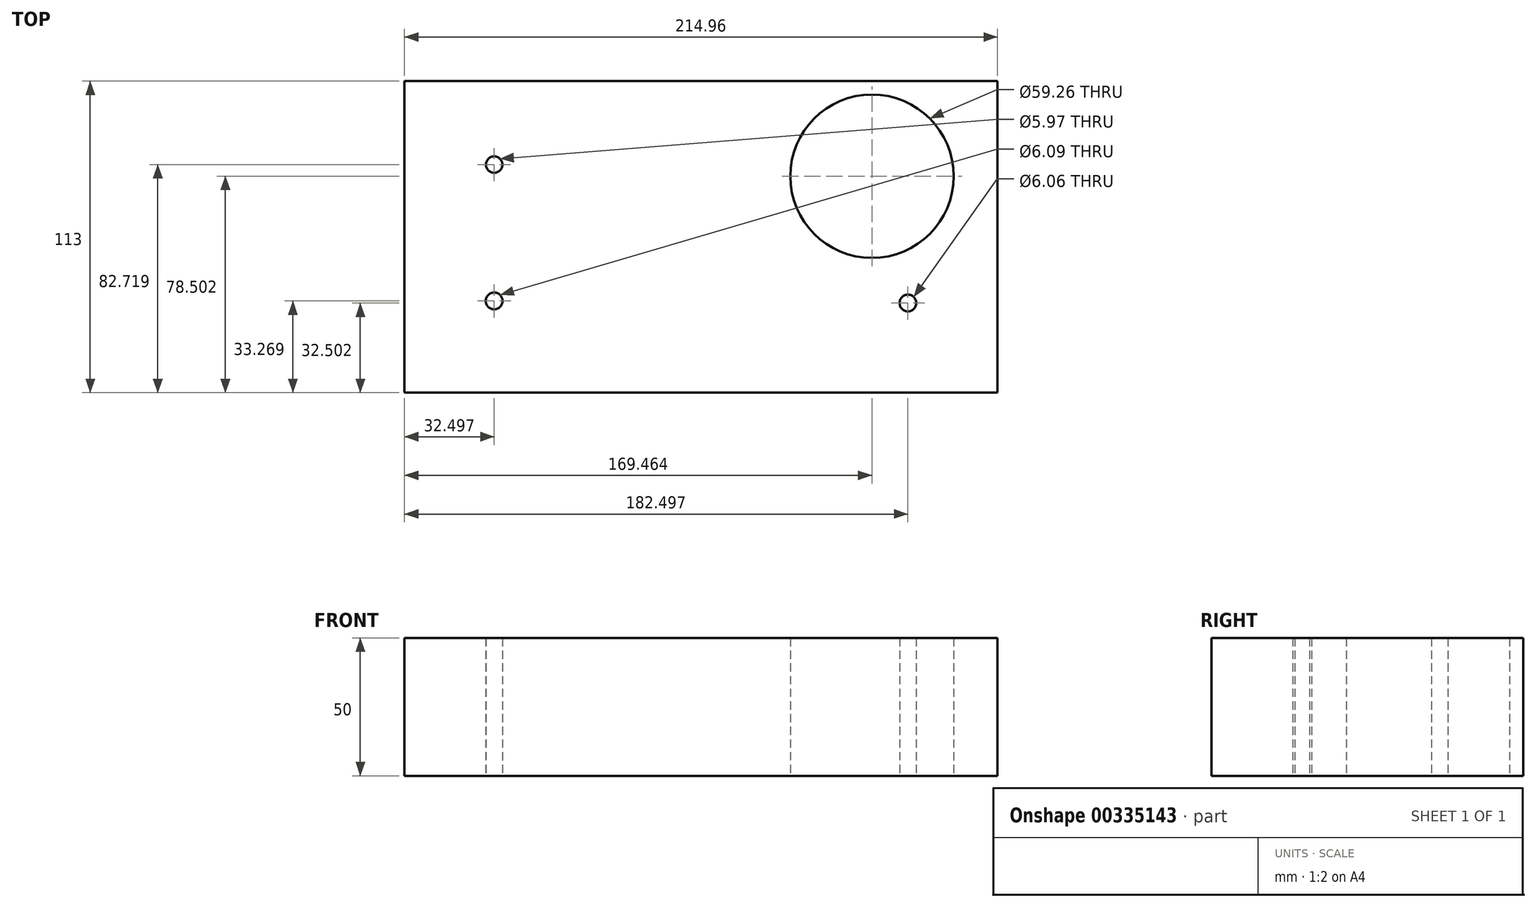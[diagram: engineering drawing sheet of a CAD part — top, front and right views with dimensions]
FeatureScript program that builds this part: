
annotation { "Feature Type Name" : "Feature", "Feature Type Description" : "" }
export const myFeature = defineFeature(function(context is Context, id is Id, definition is map)
    precondition{}
    {
        {
            var Q0;
            Q0=qCreatedBy(makeId("Top.planeOp"),FACE);
            var sketch = newSketch(context, id + "F0", { "sketchPlane" : qUnion([Q0])});
            skLineSegment(sketch, "E0.bottom", {"start": v(-82.61, -121.03) * mm, "end": v(132.35, -121.03) * mm});
            skLineSegment(sketch, "E0.top", {"start": v(-82.61, -234.03) * mm, "end": v(132.35, -234.03) * mm});
            skLineSegment(sketch, "E0.left", {"start": v(-82.61, -121.03) * mm, "end": v(-82.61, -234.03) * mm});
            skLineSegment(sketch, "E0.right", {"start": v(132.35, -121.03) * mm, "end": v(132.35, -234.03) * mm});
            skCircle(sketch, "E1", {"center": v(86.85, -155.53) * mm, "radius": 29.63 * mm});
            skCircle(sketch, "E2", {"center": v(-50.11, -151.31) * mm, "radius": 2.99 * mm});
            skCircle(sketch, "E3", {"center": v(-50.11, -200.76) * mm, "radius": 3.05 * mm});
            skCircle(sketch, "E4", {"center": v(99.89, -201.53) * mm, "radius": 3.03 * mm});
            skCircle(sketch, "E5", {"center": v(99.89, -151.03) * mm, "radius": 3.16 * mm});
            skSolve(sketch);
        }
        {
            var Q0;
            Q0 = qSketchRegion(id + "F0", true);
            extrude(context, id + "F1", {"entities" : qUnion([Q0]), "depth" : 50 * mm});
        }
    });
